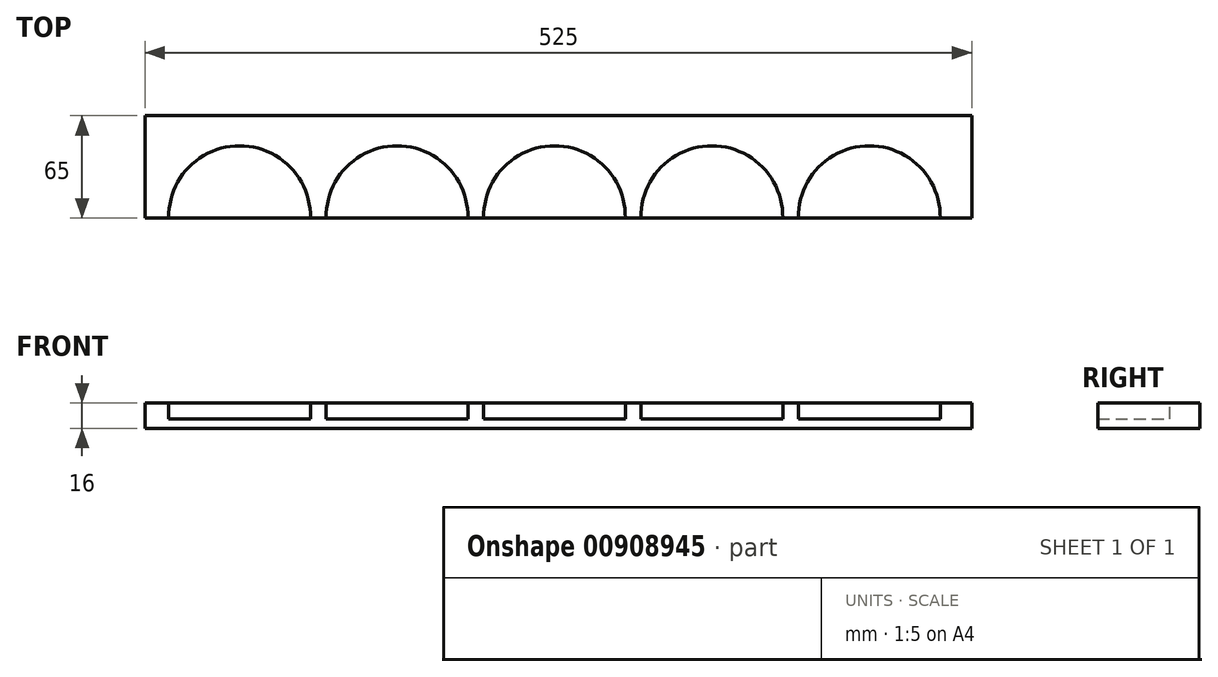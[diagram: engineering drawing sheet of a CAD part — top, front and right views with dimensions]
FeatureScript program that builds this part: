
annotation { "Feature Type Name" : "Feature", "Feature Type Description" : "" }
export const myFeature = defineFeature(function(context is Context, id is Id, definition is map)
    precondition{}
    {
        {
            var Q0;
            Q0=qCreatedBy(makeId("Front.planeOp"),FACE);
            var sketch = newSketch(context, id + "F0", { "sketchPlane" : qUnion([Q0])});
            skLineSegment(sketch, "E0.bottom", {"start": v(262.5, 8) * mm, "end": v(-262.5, 8) * mm});
            skLineSegment(sketch, "E0.top", {"start": v(262.5, -8) * mm, "end": v(-262.5, -8) * mm});
            skLineSegment(sketch, "E0.left", {"start": v(262.5, 8) * mm, "end": v(262.5, -8) * mm});
            skLineSegment(sketch, "E0.right", {"start": v(-262.5, 8) * mm, "end": v(-262.5, -8) * mm});
            skPoint(sketch, "E0.middle", {"position": v(0, 0) * mm});
            skSolve(sketch);
        }
        {
            var Q0;
            Q0=makeQuery(id+"F0.imprint","IMPRINT",FACE,{"disambiguationData":[TD([[makeQuery(id+"F0.imprint","IMPRINT",EDGE,{"derivedFrom":sQuery(id+"F0.wireOp",EDGE,"E0.bottom")}),1.0]])]});
            extrude(context, id + "F1", {"entities" : qUnion([Q0]), "oppositeDirection" : true, "depth" : 65 * mm, "offsetDistance" : 25 * mm});
        }
        {
            var Q0;
            Q0=makeQuery(id+"F1.opExtrude","SWEPT_FACE",FACE,{"disambiguationData":[OSD([sQuery(id+"F0.wireOp",EDGE,"E0.bottom")])]});
            var sketch = newSketch(context, id + "F2", { "sketchPlane" : qUnion([Q0])});
            skArc(sketch, "E1", {"start": v(-157.52, 0) * mm, "mid": v(-202.5, 45.85) * mm, "end": v(-247.5, 0) * mm});
            skArc(sketch, "E2.1.0.0", {"start": v(-57.52, 0) * mm, "mid": v(-102.5, 45.85) * mm, "end": v(-147.5, 0) * mm});
            skArc(sketch, "E2.2.0.0", {"start": v(42.48, 0) * mm, "mid": v(-2.5, 45.85) * mm, "end": v(-47.5, 0) * mm});
            skArc(sketch, "E2.3.0.0", {"start": v(142.48, 0) * mm, "mid": v(97.5, 45.85) * mm, "end": v(52.5, 0) * mm});
            skArc(sketch, "E2.4.0.0", {"start": v(242.48, 0) * mm, "mid": v(197.5, 45.85) * mm, "end": v(152.5, 0) * mm});
            skLineSegment(sketch, "E2.direction1", {"start": v(-247.5, 0) * mm, "end": v(-147.5, 0) * mm, "construction": true});
            skSolve(sketch);
        }
        {
            var Q0;
            {var subQ0=sQuery(id+"F2.wireOp",EDGE,"E1");Q0=makeQuery(id+"F2.imprint","IMPRINT",FACE,{"disambiguationData":[TD([[makeQuery(id+"F2.imprint","IMPRINT",EDGE,{"derivedFrom":subQ0}),1.0]])]});}
            var Q1;
            {var subQ0=sQuery(id+"F2.wireOp",EDGE,"E2.1.0.0");Q1=makeQuery(id+"F2.imprint","IMPRINT",FACE,{"disambiguationData":[TD([[makeQuery(id+"F2.imprint","IMPRINT",EDGE,{"derivedFrom":subQ0}),1.0]])]});}
            var Q2;
            {var subQ0=sQuery(id+"F2.wireOp",EDGE,"E2.2.0.0");Q2=makeQuery(id+"F2.imprint","IMPRINT",FACE,{"disambiguationData":[TD([[makeQuery(id+"F2.imprint","IMPRINT",EDGE,{"derivedFrom":subQ0}),1.0]])]});}
            var Q3;
            {var subQ0=sQuery(id+"F2.wireOp",EDGE,"E2.3.0.0");Q3=makeQuery(id+"F2.imprint","IMPRINT",FACE,{"disambiguationData":[TD([[makeQuery(id+"F2.imprint","IMPRINT",EDGE,{"derivedFrom":subQ0}),1.0]])]});}
            var Q4;
            {var subQ0=sQuery(id+"F2.wireOp",EDGE,"E2.4.0.0");Q4=makeQuery(id+"F2.imprint","IMPRINT",FACE,{"disambiguationData":[TD([[makeQuery(id+"F2.imprint","IMPRINT",EDGE,{"derivedFrom":subQ0}),1.0]])]});}
            extrude(context, id + "F3", {"entities" : qUnion([Q0, Q1, Q2, Q3, Q4]), "operationType" : NewBodyOperationType.REMOVE, "oppositeDirection" : true, "depth" : 10 * mm, "offsetDistance" : 25 * mm});
        }
    });
